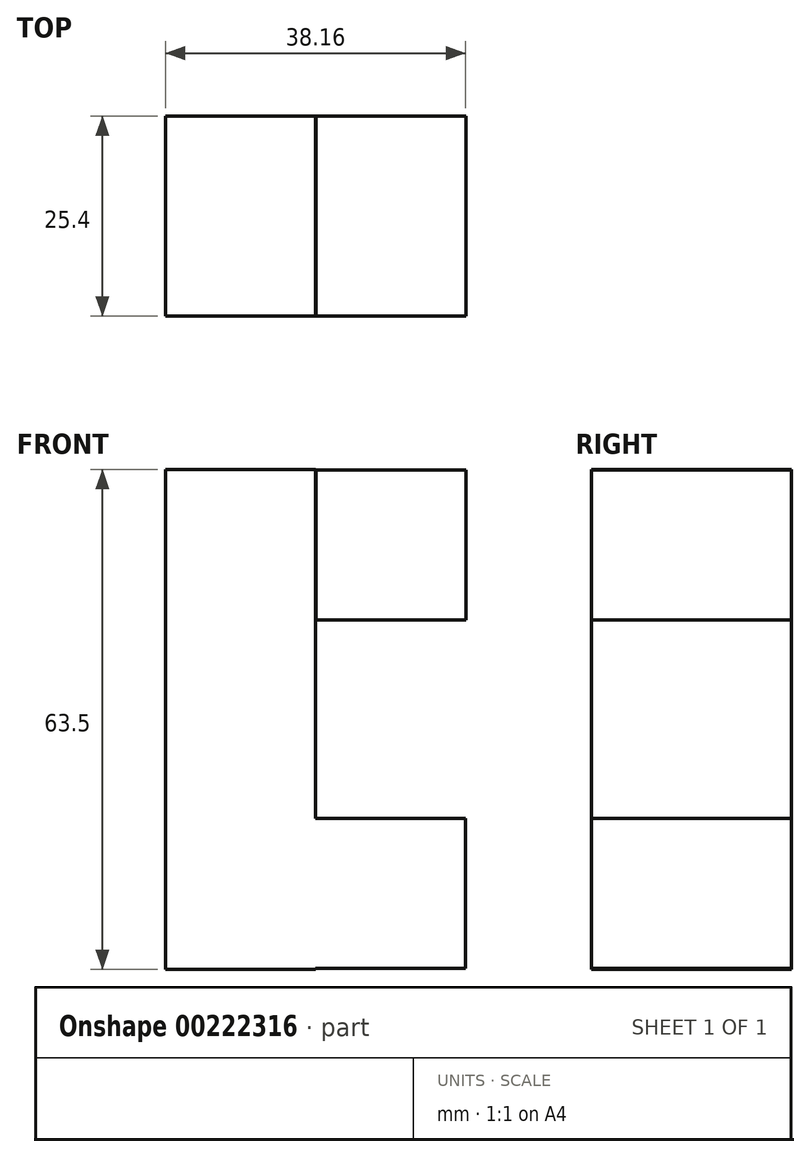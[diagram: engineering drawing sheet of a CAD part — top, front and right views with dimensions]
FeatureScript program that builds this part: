
annotation { "Feature Type Name" : "Feature", "Feature Type Description" : "" }
export const myFeature = defineFeature(function(context is Context, id is Id, definition is map)
    precondition{}
    {
        {
            var Q0;
            Q0=qCreatedBy(makeId("Front.planeOp"),FACE);
            var sketch = newSketch(context, id + "F0", { "sketchPlane" : qUnion([Q0])});
            skLineSegment(sketch, "E0.bottom", {"start": v(-38.56, 15.4) * mm, "end": v(-57.6, 15.4) * mm});
            skLineSegment(sketch, "E0.top", {"start": v(-38.56, 78.9) * mm, "end": v(-57.6, 78.9) * mm});
            skLineSegment(sketch, "E0.left", {"start": v(-38.56, 15.4) * mm, "end": v(-38.56, 78.9) * mm});
            skLineSegment(sketch, "E0.right", {"start": v(-57.6, 15.4) * mm, "end": v(-57.6, 78.9) * mm});
            skPoint(sketch, "E0.middle", {"position": v(-48.08, 47.16) * mm});
            skLineSegment(sketch, "E1.bottom", {"start": v(-19.45, 59.8) * mm, "end": v(-38.5, 59.8) * mm});
            skLineSegment(sketch, "E1.top", {"start": v(-19.45, 78.85) * mm, "end": v(-38.5, 78.85) * mm});
            skLineSegment(sketch, "E1.left", {"start": v(-19.45, 59.8) * mm, "end": v(-19.45, 78.85) * mm});
            skLineSegment(sketch, "E1.right", {"start": v(-38.5, 59.8) * mm, "end": v(-38.5, 78.85) * mm});
            skPoint(sketch, "E1.middle", {"position": v(-28.97, 69.32) * mm});
            skLineSegment(sketch, "E2.bottom", {"start": v(-19.5, 15.55) * mm, "end": v(-38.56, 15.55) * mm});
            skLineSegment(sketch, "E2.top", {"start": v(-19.5, 34.6) * mm, "end": v(-38.56, 34.6) * mm});
            skLineSegment(sketch, "E2.left", {"start": v(-19.5, 15.55) * mm, "end": v(-19.5, 34.6) * mm});
            skLineSegment(sketch, "E2.right", {"start": v(-38.56, 15.55) * mm, "end": v(-38.56, 34.6) * mm});
            skPoint(sketch, "E2.middle", {"position": v(-29.03, 25.08) * mm});
            skSolve(sketch);
        }
        {
            var Q0;
            {var subQ3=sQuery(id+"F0.wireOp",EDGE,"E0.bottom");Q0=makeQuery(id+"F0.imprint","IMPRINT",FACE,{"disambiguationData":[TD([[makeQuery(id+"F0.imprint","IMPRINT",EDGE,{"derivedFrom":subQ3}),-1.0]])]});}
            var Q1;
            Q1=makeQuery(id+"F0.imprint","IMPRINT",FACE,{"disambiguationData":[TD([[makeQuery(id+"F0.imprint","IMPRINT",EDGE,{"derivedFrom":sQuery(id+"F0.wireOp",EDGE,"E2.bottom")}),-1.0]])]});
            var Q2;
            Q2=makeQuery(id+"F0.imprint","IMPRINT",FACE,{"disambiguationData":[TD([[makeQuery(id+"F0.imprint","IMPRINT",EDGE,{"derivedFrom":sQuery(id+"F0.wireOp",EDGE,"E1.bottom")}),-1.0]])]});
            extrude(context, id + "F1", {"entities" : qUnion([Q0, Q1, Q2]), "depth" : 25.4 * mm});
        }
    });
